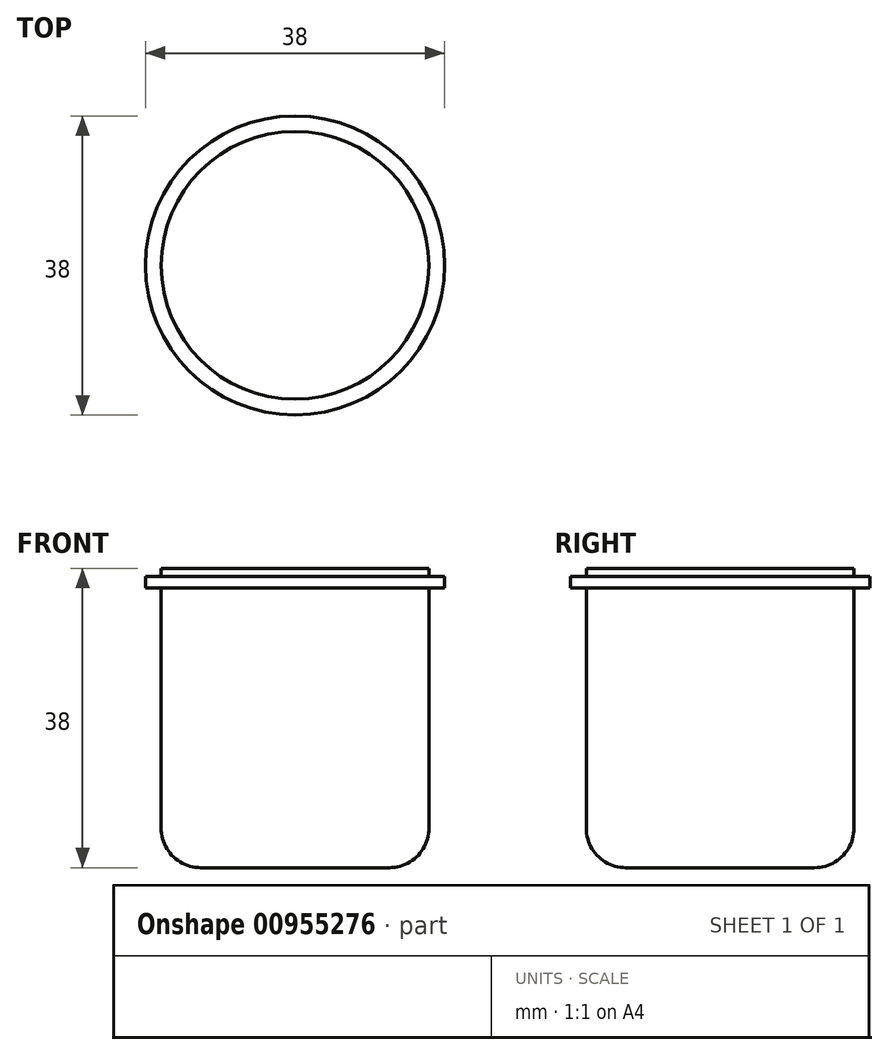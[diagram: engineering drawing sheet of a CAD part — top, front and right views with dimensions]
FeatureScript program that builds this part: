
annotation { "Feature Type Name" : "Feature", "Feature Type Description" : "" }
export const myFeature = defineFeature(function(context is Context, id is Id, definition is map)
    precondition{}
    {
        {
            var Q0;
            Q0=qCreatedBy(makeId("Top.planeOp"),FACE);
            var sketch = newSketch(context, id + "F0", { "sketchPlane" : qUnion([Q0])});
            skCircle(sketch, "E0", {"center": v(0, 0) * mm, "radius": 17 * mm});
            skSolve(sketch);
        }
        {
            var Q0;
            Q0=makeQuery(id+"F0.imprint","IMPRINT",FACE,{"disambiguationData":[TD([[makeQuery(id+"F0.imprint","IMPRINT",EDGE,{"derivedFrom":sQuery(id+"F0.wireOp",EDGE,"E0")}),1.0]])]});
            extrude(context, id + "F1", {"entities" : qUnion([Q0]), "depth" : 38 * mm, "offsetDistance" : 25 * mm});
        }
        {
            var Q0;
            Q0=makeQuery(id+"F1.opExtrude","CAP_EDGE",EDGE,{"disambiguationData":[OSD([sQuery(id+"F0.wireOp",EDGE,"E0")])],"isStart":true});
            fillet(context, id + "F2", {"entities" : qUnion([Q0]), "radius" : 5 * mm, "tangentPropagation" : true, "allowEdgeOverflow" : false});
        }
        {
            var Q0;
            Q0=makeQuery(id+"F1.opExtrude","CAP_FACE",FACE,{"disambiguationData":[OSD([sQuery(id+"F0.wireOp",EDGE,"E0")])],"isStart":false});
            cPlane(context, id + "F3", {"entities" : qUnion([Q0]), "cplaneType" : CPlaneType.OFFSET, "offset" : 1 * mm, "oppositeDirection" : true, "width" : 150 * mm, "height" : 150 * mm});
        }
        {
            var Q0;
            Q0=qCreatedBy(id+"F3.planeOp",FACE);
            var sketch = newSketch(context, id + "F4", { "sketchPlane" : qUnion([Q0])});
            skCircle(sketch, "E1", {"center": v(0, 0) * mm, "radius": 19 * mm});
            skSolve(sketch);
        }
        {
            var Q0;
            Q0=qSketchRegion(id+"F4",true);
            extrude(context, id + "F5", {"entities" : qUnion([Q0]), "operationType" : NewBodyOperationType.ADD, "oppositeDirection" : true, "depth" : 1.5 * mm, "offsetDistance" : 25 * mm});
        }
    });
